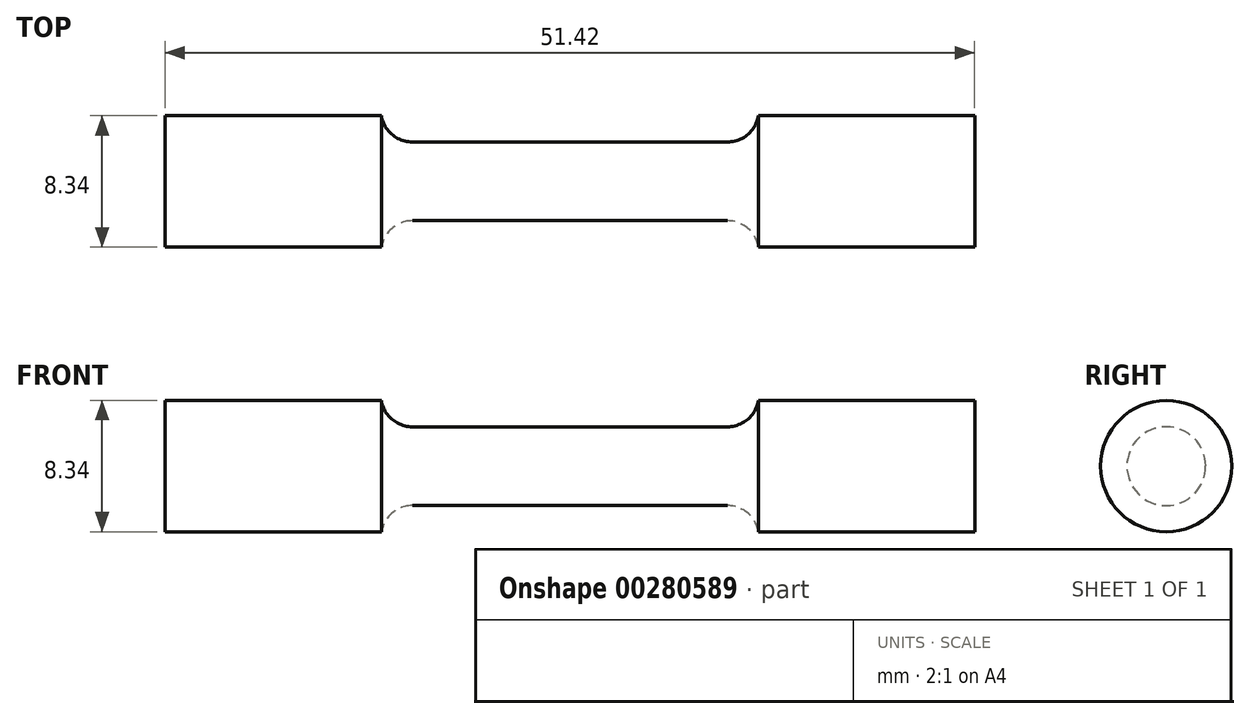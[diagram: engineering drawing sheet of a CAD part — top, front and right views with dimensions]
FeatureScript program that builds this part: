
annotation { "Feature Type Name" : "Feature", "Feature Type Description" : "" }
export const myFeature = defineFeature(function(context is Context, id is Id, definition is map)
    precondition{}
    {
        {
            var Q0;
            Q0=qCreatedBy(makeId("Front.planeOp"),FACE);
            var sketch = newSketch(context, id + "F0", { "sketchPlane" : qUnion([Q0])});
            skLineSegment(sketch, "E0", {"start": v(0, 2.5) * mm, "end": v(10, 2.5) * mm});
            skArc(sketch, "E1", {"start": v(10, 2.5) * mm, "mid": v(11.3, 2.97) * mm, "end": v(11.97, 4.17) * mm});
            skLineSegment(sketch, "E2", {"start": v(11.97, 4.17) * mm, "end": v(25.71, 4.17) * mm});
            skLineSegment(sketch, "E3", {"start": v(25.71, 4.17) * mm, "end": v(25.71, 0) * mm});
            skLineSegment(sketch, "E4.MirrorCS", {"start": v(0, 2.5) * mm, "end": v(-10, 2.5) * mm});
            skLineSegment(sketch, "E5.MirrorCS", {"start": v(-25.71, 4.17) * mm, "end": v(-25.71, 0) * mm});
            skLineSegment(sketch, "E6.MirrorCS", {"start": v(-11.97, 4.17) * mm, "end": v(-25.71, 4.17) * mm});
            skArc(sketch, "E7.MirrorCS", {"start": v(-10, 2.5) * mm, "mid": v(-11.3, 2.97) * mm, "end": v(-11.97, 4.17) * mm});
            skLineSegment(sketch, "E8", {"start": v(-25.71, 0) * mm, "end": v(25.71, 0) * mm});
            skSolve(sketch);
        }
        {
            var Q0;
            Q0 = qSketchRegion(id + "F0", true);
            var Q1;
            Q1=sQuery(id+"F0.wireOp",EDGE,"E8");
            revolve(context, id + "F1", {"entities" : qUnion([Q0]), "axis" : qUnion([Q1]), "revolveType" : RevolveType.FULL});
        }
    });
